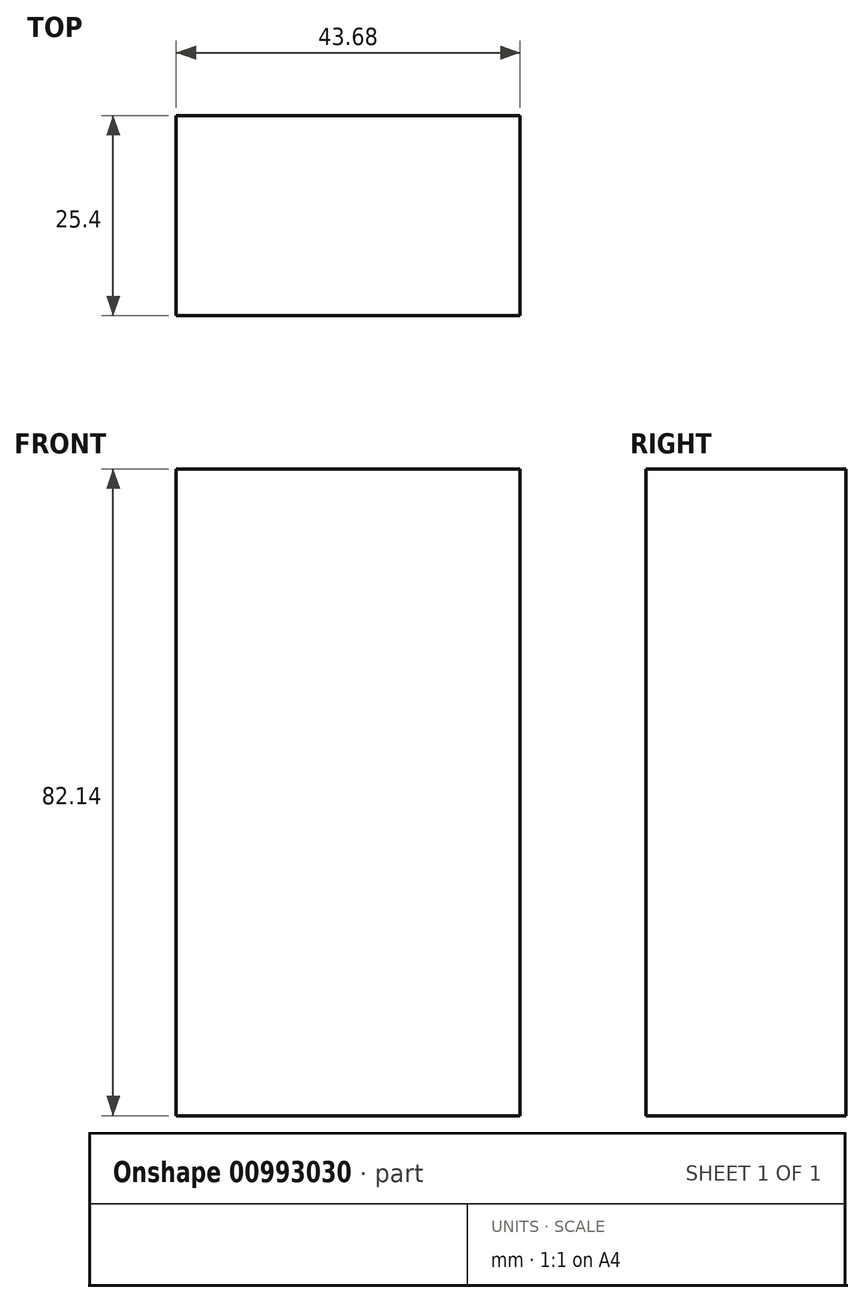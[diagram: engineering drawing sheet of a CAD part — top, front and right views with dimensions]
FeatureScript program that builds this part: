
annotation { "Feature Type Name" : "Feature", "Feature Type Description" : "" }
export const myFeature = defineFeature(function(context is Context, id is Id, definition is map)
    precondition{}
    {
        {
            var Q0;
            Q0=qCreatedBy(makeId("Front.planeOp"),FACE);
            var sketch = newSketch(context, id + "F0", { "sketchPlane" : qUnion([Q0])});
            skLineSegment(sketch, "E0.bottom", {"start": v(-108.66, 244.06) * mm, "end": v(-64.98, 244.06) * mm});
            skLineSegment(sketch, "E0.top", {"start": v(-108.66, 161.92) * mm, "end": v(-64.98, 161.92) * mm});
            skLineSegment(sketch, "E0.left", {"start": v(-108.66, 244.06) * mm, "end": v(-108.66, 161.92) * mm});
            skLineSegment(sketch, "E0.right", {"start": v(-64.98, 244.06) * mm, "end": v(-64.98, 161.92) * mm});
            skLineSegment(sketch, "E1.1.0.0", {"start": v(-83.26, 161.92) * mm, "end": v(-39.58, 161.92) * mm});
            skLineSegment(sketch, "E1.2.0.0", {"start": v(-57.86, 161.92) * mm, "end": v(-14.18, 161.92) * mm});
            skLineSegment(sketch, "E1.direction1", {"start": v(0, 0) * mm, "end": v(25.4, 0) * mm, "construction": true});
            skSolve(sketch);
        }
        {
            var Q0;
            Q0 = qSketchRegion(id + "F0", true);
            extrude(context, id + "F1", {"entities" : qUnion([Q0]), "depth" : 25.4 * mm, "offsetDistance" : 25.4 * mm});
        }
    });
